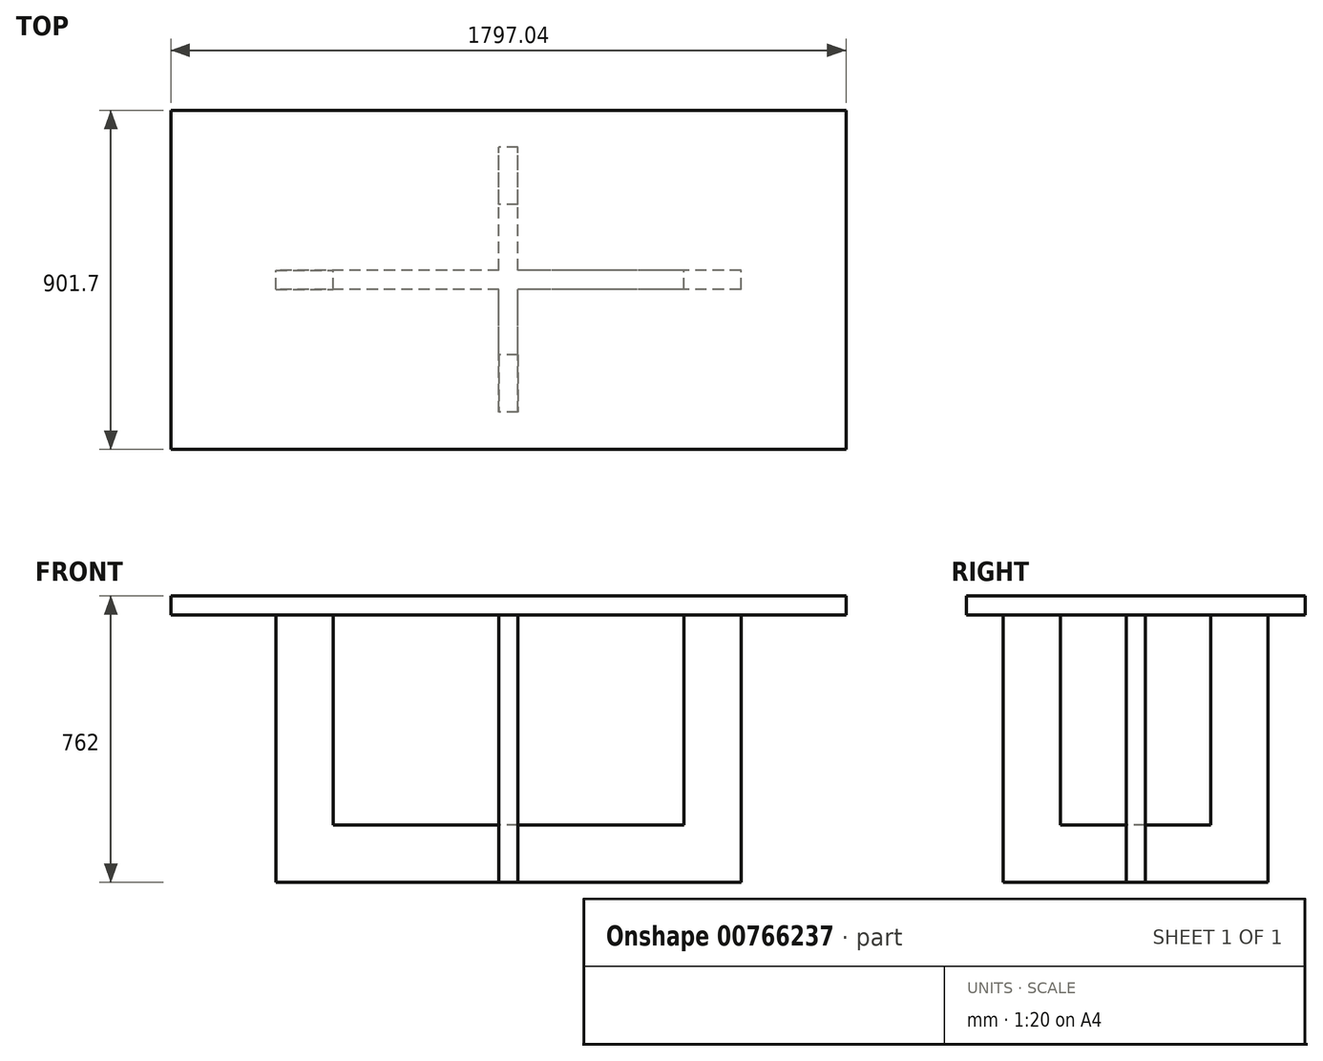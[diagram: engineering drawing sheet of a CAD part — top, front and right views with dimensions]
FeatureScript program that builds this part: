
annotation { "Feature Type Name" : "Feature", "Feature Type Description" : "" }
export const myFeature = defineFeature(function(context is Context, id is Id, definition is map)
    precondition{}
    {
        {
            var Q0;
            Q0=qCreatedBy(makeId("Top.planeOp"),FACE);
            var sketch = newSketch(context, id + "F0", { "sketchPlane" : qUnion([Q0])});
            skLineSegment(sketch, "E0.bottom", {"start": v(898.53, -450.85) * mm, "end": v(-898.53, -450.85) * mm});
            skLineSegment(sketch, "E0.top", {"start": v(898.52, 450.85) * mm, "end": v(-898.53, 450.85) * mm});
            skLineSegment(sketch, "E0.left", {"start": v(898.53, -450.85) * mm, "end": v(898.52, 450.85) * mm});
            skLineSegment(sketch, "E0.right", {"start": v(-898.52, -450.85) * mm, "end": v(-898.53, 450.85) * mm});
            skPoint(sketch, "E0.middle", {"position": v(0, 0) * mm});
            skSolve(sketch);
        }
        {
            var Q0;
            Q0=makeQuery(id+"F0.imprint","IMPRINT",FACE,{"disambiguationData":[TD([[makeQuery(id+"F0.imprint","IMPRINT",EDGE,{"derivedFrom":sQuery(id+"F0.wireOp",EDGE,"E0.bottom")}),-1.0]])]});
            extrude(context, id + "F1", {"entities" : qUnion([Q0]), "depth" : 50.8 * mm, "offsetDistance" : 25.4 * mm});
        }
        {
            var Q0;
            Q0=makeQuery(id+"F1.opExtrude","CAP_FACE",FACE,{"disambiguationData":[OSD([sQuery(id+"F0.wireOp",EDGE,"E0.bottom"),sQuery(id+"F0.wireOp",EDGE,"E0.top"),sQuery(id+"F0.wireOp",EDGE,"E0.left"),sQuery(id+"F0.wireOp",EDGE,"E0.right")])],"isStart":true});
            var sketch = newSketch(context, id + "F2", { "sketchPlane" : qUnion([Q0])});
            skLineSegment(sketch, "E1.bottom", {"start": v(619.13, 25.4) * mm, "end": v(466.73, 25.4) * mm});
            skLineSegment(sketch, "E1.top", {"start": v(619.13, -25.4) * mm, "end": v(466.73, -25.4) * mm});
            skLineSegment(sketch, "E1.left", {"start": v(619.13, 25.4) * mm, "end": v(619.13, -25.4) * mm});
            skLineSegment(sketch, "E1.right", {"start": v(466.73, 25.4) * mm, "end": v(466.73, -25.4) * mm});
            skPoint(sketch, "E1.middle", {"position": v(542.93, 0) * mm});
            skSolve(sketch);
        }
        {
            var Q0;
            Q0=qCreatedBy(makeId("Front.planeOp"),FACE);
            var sketch = newSketch(context, id + "F3", { "sketchPlane" : qUnion([Q0])});
            skPoint(sketch, "E2.0", {"position": v(542.93, 0) * mm});
            skLineSegment(sketch, "E3", {"start": v(542.93, 0) * mm, "end": v(542.93, -635) * mm});
            skLineSegment(sketch, "E4", {"start": v(542.92, -635) * mm, "end": v(-542.93, -635) * mm});
            skLineSegment(sketch, "E5", {"start": v(-542.93, -635) * mm, "end": v(-542.93, 0) * mm});
            skSolve(sketch);
        }
        {
            var Q0;
            Q0=makeQuery(id+"F2.imprint","IMPRINT",FACE,{"disambiguationData":[TD([[makeQuery(id+"F2.imprint","IMPRINT",EDGE,{"derivedFrom":sQuery(id+"F2.wireOp",EDGE,"E1.bottom")}),1.0]])]});
            var Q1;
            Q1=sQuery(id+"F3.wireOp",EDGE,"E3");
            var Q2;
            Q2=sQuery(id+"F3.wireOp",EDGE,"E4");
            var Q3;
            Q3=sQuery(id+"F3.wireOp",EDGE,"E5");
            sweep(context, id + "F4", {"operationType" : NewBodyOperationType.ADD, "profiles" : qUnion([Q0]), "path" : qUnion([Q1, Q2, Q3])});
        }
        {
            var Q0;
            Q0=makeQuery(id+"F1.opExtrude","CAP_FACE",FACE,{"disambiguationData":[OSD([sQuery(id+"F0.wireOp",EDGE,"E0.bottom"),sQuery(id+"F0.wireOp",EDGE,"E0.top"),sQuery(id+"F0.wireOp",EDGE,"E0.left"),sQuery(id+"F0.wireOp",EDGE,"E0.right")])],"isStart":true});
            var sketch = newSketch(context, id + "F5", { "sketchPlane" : qUnion([Q0])});
            skLineSegment(sketch, "E6.bottom", {"start": v(25.4, 200.03) * mm, "end": v(-25.4, 200.03) * mm});
            skLineSegment(sketch, "E6.top", {"start": v(25.4, 352.43) * mm, "end": v(-25.4, 352.43) * mm});
            skLineSegment(sketch, "E6.left", {"start": v(25.4, 200.03) * mm, "end": v(25.4, 352.43) * mm});
            skLineSegment(sketch, "E6.right", {"start": v(-25.4, 200.03) * mm, "end": v(-25.4, 352.43) * mm});
            skPoint(sketch, "E6.middle", {"position": v(0, 276.23) * mm});
            skSolve(sketch);
        }
        {
            var Q0;
            Q0=qCreatedBy(makeId("Right.planeOp"),FACE);
            var sketch = newSketch(context, id + "F6", { "sketchPlane" : qUnion([Q0])});
            skPoint(sketch, "E7.0", {"position": v(-276.23, 0) * mm});
            skLineSegment(sketch, "E8", {"start": v(-276.23, 0) * mm, "end": v(-276.23, -635) * mm});
            skLineSegment(sketch, "E9", {"start": v(-276.22, -635) * mm, "end": v(276.23, -635) * mm});
            skLineSegment(sketch, "E10", {"start": v(276.23, -635) * mm, "end": v(276.23, 0) * mm});
            skSolve(sketch);
        }
        {
            var Q0;
            Q0=makeQuery(id+"F5.imprint","IMPRINT",FACE,{"disambiguationData":[TD([[makeQuery(id+"F5.imprint","IMPRINT",EDGE,{"derivedFrom":sQuery(id+"F5.wireOp",EDGE,"E6.bottom")}),-1.0]])]});
            var Q1;
            Q1=sQuery(id+"F6.wireOp",EDGE,"E8");
            var Q2;
            Q2=sQuery(id+"F6.wireOp",EDGE,"E9");
            var Q3;
            Q3=sQuery(id+"F6.wireOp",EDGE,"E10");
            sweep(context, id + "F7", {"operationType" : NewBodyOperationType.ADD, "profiles" : qUnion([Q0]), "path" : qUnion([Q1, Q2, Q3])});
        }
    });
